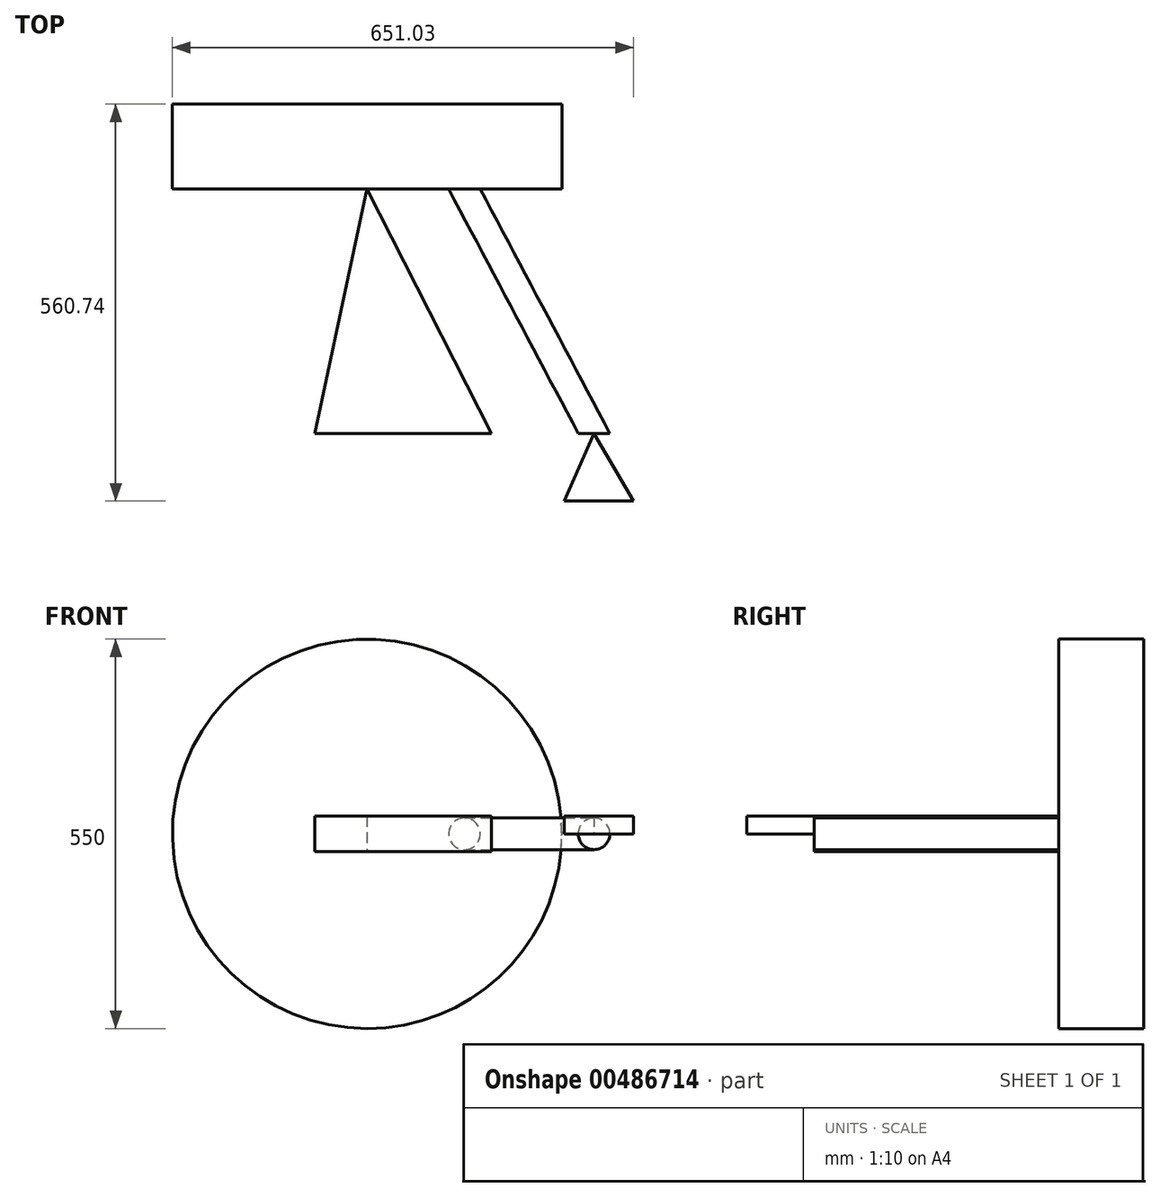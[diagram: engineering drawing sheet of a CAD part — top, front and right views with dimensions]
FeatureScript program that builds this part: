
annotation { "Feature Type Name" : "Feature", "Feature Type Description" : "" }
export const myFeature = defineFeature(function(context is Context, id is Id, definition is map)
    precondition{}
    {
        {
            var Q0;
            Q0=qCreatedBy(makeId("Top.planeOp"),FACE);
            var sketch = newSketch(context, id + "F0", { "sketchPlane" : qUnion([Q0])});
            skLineSegment(sketch, "E0", {"start": v(0, 0) * mm, "end": v(-175.79, 345) * mm});
            skLineSegment(sketch, "E1", {"start": v(-175.79, 345) * mm, "end": v(-250, 0) * mm});
            skLineSegment(sketch, "E2", {"start": v(-250, 0) * mm, "end": v(0, 0) * mm});
            skLineSegment(sketch, "E3.bottom", {"start": v(99.21, 345) * mm, "end": v(-175.79, 345) * mm});
            skLineSegment(sketch, "E3.top", {"start": v(99.21, 465) * mm, "end": v(-175.79, 465) * mm});
            skLineSegment(sketch, "E3.left", {"start": v(99.21, 345) * mm, "end": v(99.21, 465) * mm});
            skLineSegment(sketch, "E3.right", {"start": v(-175.79, 345) * mm, "end": v(-175.79, 465) * mm});
            skPoint(sketch, "E4.startSnap0", {"position": v(-38.29, 465) * mm});
            skPoint(sketch, "E4.endSnap0", {"position": v(-175.79, 345) * mm});
            skPoint(sketch, "E5", {"position": v(-38.29, 345) * mm});
            skLineSegment(sketch, "E6", {"start": v(-38.29, 345) * mm, "end": v(144.76, 0) * mm});
            skLineSegment(sketch, "E7", {"start": v(0, 0) * mm, "end": v(251.42, 0) * mm});
            skPoint(sketch, "E8", {"position": v(144.76, 0) * mm});
            skLineSegment(sketch, "E9", {"start": v(144.76, 0) * mm, "end": v(102.74, -95.74) * mm});
            skLineSegment(sketch, "E10", {"start": v(102.74, -95.74) * mm, "end": v(200.24, -95.74) * mm});
            skLineSegment(sketch, "E11", {"start": v(200.24, -95.74) * mm, "end": v(144.76, 0) * mm});
            skSolve(sketch);
        }
        {
            var Q0;
            Q0=makeQuery(id+"F0.imprint","IMPRINT",FACE,{"disambiguationData":[TD([[makeQuery(id+"F0.imprint","IMPRINT",EDGE,{"derivedFrom":sQuery(id+"F0.wireOp",EDGE,"E3.bottom")}),-1.0]])]});
            var Q1;
            Q1=sQuery(id+"F0.wireOp",EDGE,"E3.right");
            revolve(context, id + "F1", {"entities" : qUnion([Q0]), "axis" : qUnion([Q1]), "revolveType" : RevolveType.FULL});
        }
        {
            var Q0;
            Q0=makeQuery(id+"F0.imprint","IMPRINT",FACE,{"disambiguationData":[TD([[makeQuery(id+"F0.imprint","IMPRINT",EDGE,{"derivedFrom":sQuery(id+"F0.wireOp",EDGE,"E0")}),1.0]])]});
            extrude(context, id + "F2", {"entities" : qUnion([Q0]), "endBound" : BoundingType.SYMMETRIC, "depth" : 50 * mm});
        }
        {
            var Q0;
            Q0=makeQuery(id+"F1.opRevolve","SWEPT_FACE",FACE,{"disambiguationData":[OSD([sQuery(id+"F0.wireOp",EDGE,"E3.bottom")])]});
            var sketch = newSketch(context, id + "F3", { "sketchPlane" : qUnion([Q0])});
            skLineSegment(sketch, "E12", {"start": v(-175.79, 0) * mm, "end": v(-175.79, -168.5) * mm, "construction": true});
            skLineSegment(sketch, "E13", {"start": v(-37.22, 0) * mm, "end": v(-37.22, -174.07) * mm, "construction": true});
            skSolve(sketch);
        }
        {
            var Q0;
            Q0=qCreatedBy(makeId("Front.planeOp"),FACE);
            var sketch = newSketch(context, id + "F4", { "sketchPlane" : qUnion([Q0])});
            skCircle(sketch, "E14", {"center": v(144.77, 0) * mm, "radius": 22.31 * mm});
            skSolve(sketch);
        }
        {
            var Q0;
            Q0=makeQuery(id+"F4.imprint","IMPRINT",FACE,{"disambiguationData":[TD([[makeQuery(id+"F4.imprint","IMPRINT",EDGE,{"derivedFrom":sQuery(id+"F4.wireOp",EDGE,"E14")}),1.0]])]});
            var Q1;
            Q1=sQuery(id+"F0.wireOp",EDGE,"E6");
            sweep(context, id + "F5", {"profiles" : qUnion([Q0]), "path" : qUnion([Q1])});
        }
        {
            var Q0;
            Q0=makeQuery(id+"F5.opSweep","CAP_FACE",FACE,{"disambiguationData":[OSD([sQuery(id+"F0.wireOp",VERTEX,"E6.end"),sQuery(id+"F4.wireOp",EDGE,"E14")])],"isStart":true});
            var sketch = newSketch(context, id + "F6", { "sketchPlane" : qUnion([Q0])});
            skLineSegment(sketch, "E15", {"start": v(144.77, 0) * mm, "end": v(144.77, -61.74) * mm, "construction": true});
            skSolve(sketch);
        }
        {
            var Q0;
            {var subQ0=sQuery(id+"F0.wireOp",EDGE,"E9");Q0=makeQuery(id+"F0.imprint","IMPRINT",FACE,{"disambiguationData":[TD([[makeQuery(id+"F0.imprint","IMPRINT",EDGE,{"derivedFrom":subQ0}),1.0]])]});}
            extrude(context, id + "F7", {"entities" : qUnion([Q0]), "depth" : 25 * mm});
        }
    });
